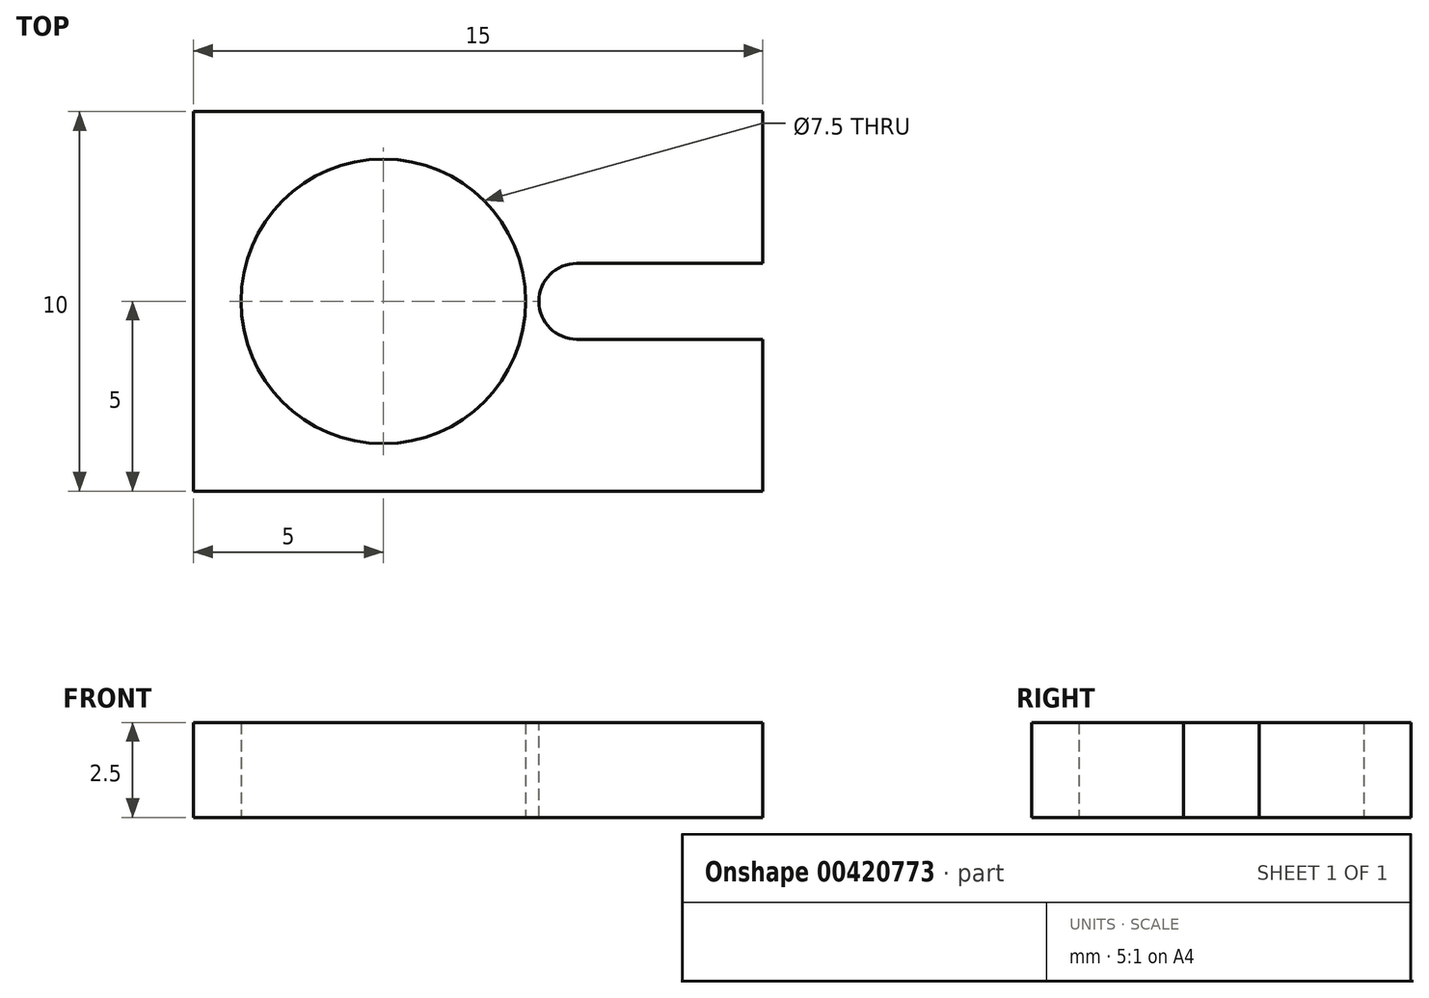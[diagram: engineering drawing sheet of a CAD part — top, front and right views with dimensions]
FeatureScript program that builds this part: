
annotation { "Feature Type Name" : "Feature", "Feature Type Description" : "" }
export const myFeature = defineFeature(function(context is Context, id is Id, definition is map)
    precondition{}
    {
        {
            var Q0;
            Q0=qCreatedBy(makeId("Top.planeOp"),FACE);
            var sketch = newSketch(context, id + "F0", { "sketchPlane" : qUnion([Q0])});
            skLineSegment(sketch, "E0.bottom", {"start": v(-5, 5) * mm, "end": v(10, 5) * mm});
            skLineSegment(sketch, "E0.top", {"start": v(-5, -5) * mm, "end": v(10, -5) * mm});
            skLineSegment(sketch, "E0.left", {"start": v(-5, 5) * mm, "end": v(-5, -5) * mm});
            skLineSegment(sketch, "E0.right", {"start": v(10, 5) * mm, "end": v(10, -5) * mm});
            skCircle(sketch, "E1", {"center": v(0, 0) * mm, "radius": 3.75 * mm});
            skLineSegment(sketch, "E2.right", {"start": v(10, 2.5) * mm, "end": v(10, -2.5) * mm});
            skLineSegment(sketch, "E3.bottom", {"start": v(10, 1) * mm, "end": v(4.1, 1) * mm});
            skLineSegment(sketch, "E3.top", {"start": v(10, -1) * mm, "end": v(4.1, -1) * mm});
            skLineSegment(sketch, "E3.left", {"start": v(10, 1) * mm, "end": v(10, -1) * mm});
            skLineSegment(sketch, "E3.right", {"start": v(4.1, 1) * mm, "end": v(4.1, -1) * mm});
            skSolve(sketch);
        }
        {
            var Q0;
            {var subQ8=sQuery(id+"F0.wireOp",EDGE,"E0.bottom");Q0=makeQuery(id+"F0.imprint","IMPRINT",FACE,{"disambiguationData":[TD([[makeQuery(id+"F0.imprint","IMPRINT",EDGE,{"derivedFrom":subQ8}),-1.0]])]});}
            extrude(context, id + "F1", {"entities" : qUnion([Q0]), "depth" : 2.5 * mm});
        }
        {
            var Q0;
            Q0=makeQuery(id+"F1.opExtrude","SWEPT_EDGE",EDGE,{"disambiguationData":[OSD([sQuery(id+"F0.wireOp",EDGE,"E3.bottom"),sQuery(id+"F0.wireOp",EDGE,"E3.right")])]});
            fillet(context, id + "F2", {"entities" : qUnion([Q0]), "radius" : 1 * mm, "tangentPropagation" : true, "allowEdgeOverflow" : false});
        }
        {
            var Q0;
            Q0=makeQuery(id+"F1.opExtrude","SWEPT_EDGE",EDGE,{"disambiguationData":[OSD([sQuery(id+"F0.wireOp",EDGE,"E3.top"),sQuery(id+"F0.wireOp",EDGE,"E3.right")])]});
            fillet(context, id + "F3", {"entities" : qUnion([Q0]), "radius" : 1 * mm, "tangentPropagation" : true, "allowEdgeOverflow" : false});
        }
    });
